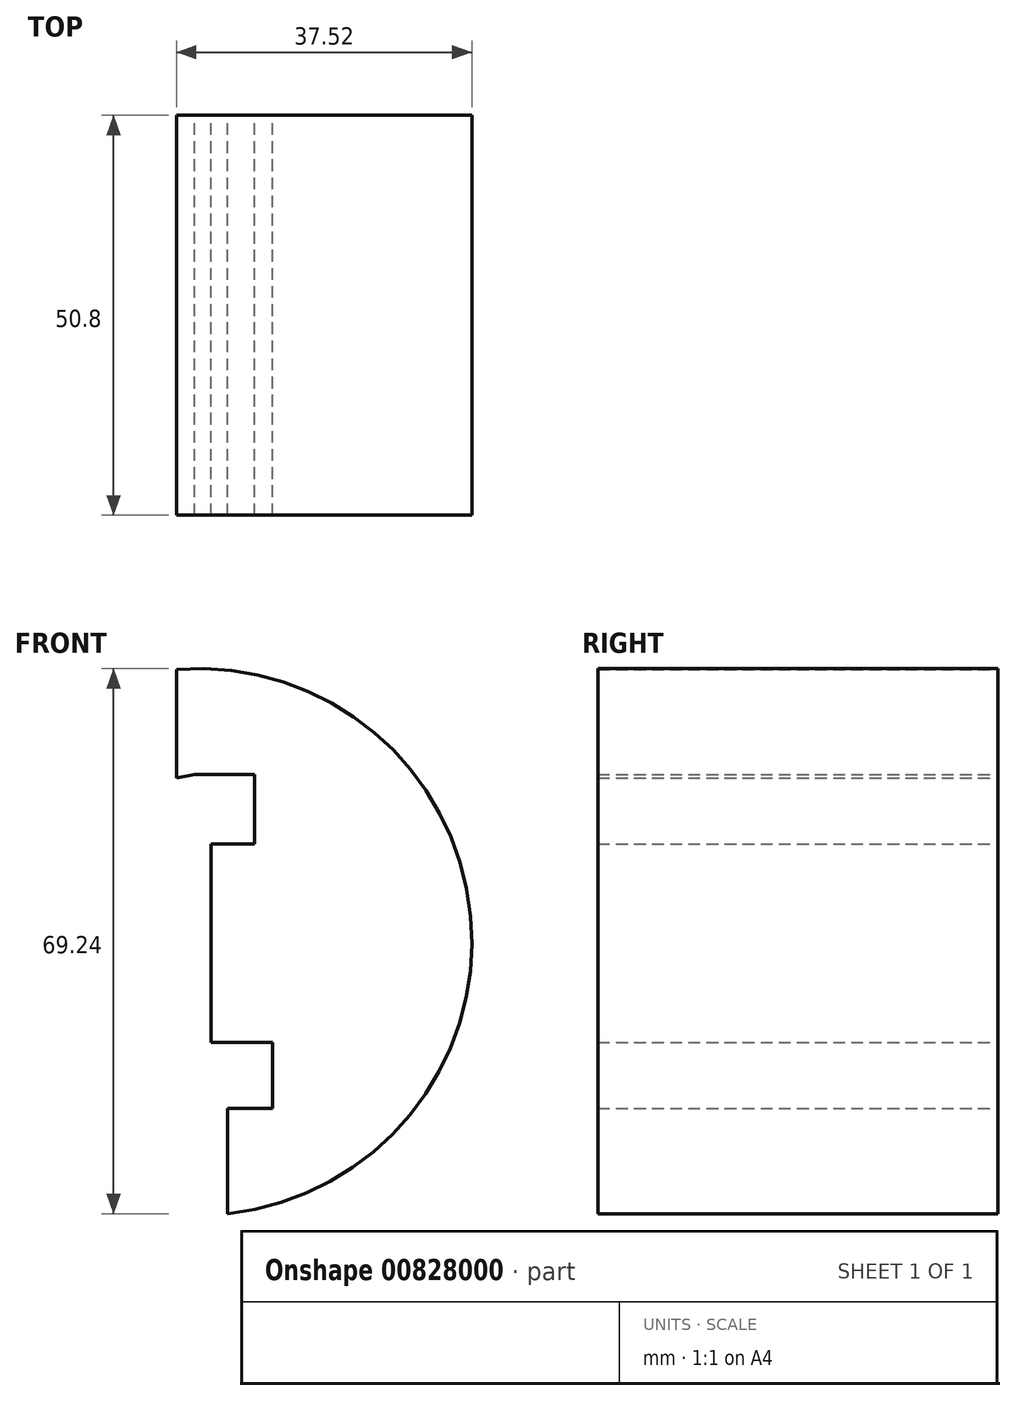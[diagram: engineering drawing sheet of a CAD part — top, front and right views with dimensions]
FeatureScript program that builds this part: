
annotation { "Feature Type Name" : "Feature", "Feature Type Description" : "" }
export const myFeature = defineFeature(function(context is Context, id is Id, definition is map)
    precondition{}
    {
        {
            var Q0;
            Q0=qCreatedBy(makeId("Front.planeOp"),FACE);
            var sketch = newSketch(context, id + "F0", { "sketchPlane" : qUnion([Q0])});
            skArc(sketch, "E0", {"start": v(14.99, -26.07) * mm, "mid": v(45.86, 11.7) * mm, "end": v(8.5, 43.06) * mm});
            skLineSegment(sketch, "E1", {"start": v(14.99, -26.07) * mm, "end": v(14.99, -12.7) * mm});
            skLineSegment(sketch, "E2", {"start": v(14.99, -12.7) * mm, "end": v(20.72, -12.7) * mm});
            skLineSegment(sketch, "E3", {"start": v(20.72, -12.7) * mm, "end": v(20.72, -4.3) * mm});
            skLineSegment(sketch, "E4", {"start": v(20.72, -4.3) * mm, "end": v(12.89, -4.3) * mm});
            skLineSegment(sketch, "E5", {"start": v(12.89, -4.3) * mm, "end": v(12.89, 20.9) * mm});
            skLineSegment(sketch, "E6", {"start": v(12.89, 20.9) * mm, "end": v(18.43, 20.9) * mm});
            skLineSegment(sketch, "E7", {"start": v(18.43, 20.9) * mm, "end": v(18.43, 29.7) * mm});
            skLineSegment(sketch, "E8", {"start": v(18.43, 29.7) * mm, "end": v(10.79, 29.7) * mm});
            skLineSegment(sketch, "E9", {"start": v(10.79, 29.7) * mm, "end": v(8.5, 43.06) * mm});
            skLineSegment(sketch, "E10", {"start": v(10.79, 29.7) * mm, "end": v(8.5, 29.3) * mm});
            skLineSegment(sketch, "E11", {"start": v(8.5, 29.3) * mm, "end": v(8.5, 43.06) * mm});
            skSolve(sketch);
        }
        {
            var Q0;
            Q0 = qSketchRegion(id + "F0", true);
            extrude(context, id + "F1", {"entities" : qUnion([Q0]), "depth" : 50.8 * mm, "offsetDistance" : 25.4 * mm});
        }
    });
